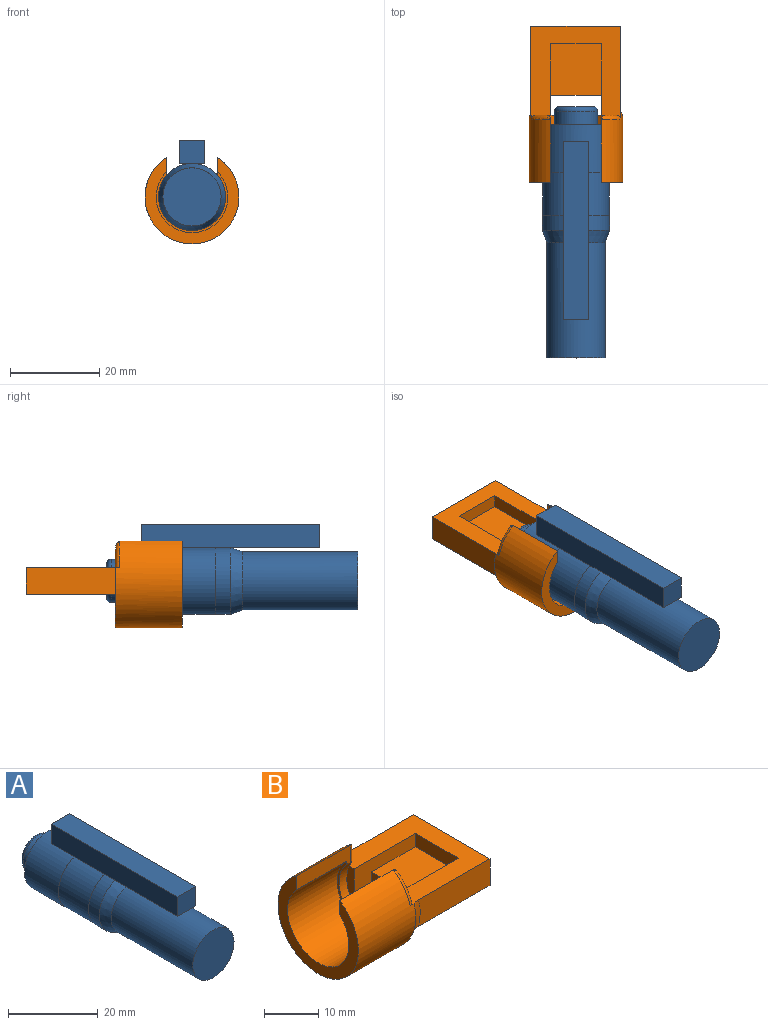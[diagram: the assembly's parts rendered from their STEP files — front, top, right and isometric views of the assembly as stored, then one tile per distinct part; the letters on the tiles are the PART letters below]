
ASSEMBLY  parts=2 mates=1
PART A: 18 faces, bbox 15x56.2x20.2 mm
  f0: cylinder r=7.5mm len=15mm, axis (0,1,0), area 487.2mm2, adj f1,f9,f12,f13
  f1: plane 15x14.9mm, normal (0,-1,0), area 3.4mm2, adj f0,f2,f12
  f2: cylinder r=7.42mm len=14.85mm, axis (0,1,0), area 433.9mm2, adj f1,f4,f12
  f3: cylinder r=7.5mm len=15mm, axis (0,1,0), area 149.7mm2, adj f4,f5,f12
  f4: plane 15x14.9mm, normal (0,1,0), area 3.4mm2, adj f2,f3,f12
  f5: cone r=7.5mm half-angle=20deg, axis (0,1,0), area 128.2mm2, adj f3,f10,f12
  f6: cylinder r=4.83mm len=9.65mm, axis (0,1,0), area 92.5mm2, adj f8,f9
  f7: plane 7.65x7.65mm, normal (0,1,0), area 46mm2, adj f8
  f8: torus R=3.82mm, axis (0,-1,0), area 44mm2, adj f6,f7
  f9: plane 15x15mm, normal (0,1,0), area 103.6mm2, adj f0,f6
  f10: cylinder r=6.5mm len=25.8mm, axis (0,1,0), area 1053.7mm2, adj f5,f11
  f11: plane 13x13mm, normal (0,-1,0), area 132.7mm2, adj f10
  f12: plane 39.9x5.75mm, normal (0,0,-1), area 192.2mm2, adj f0,f1,f2,f3,f4,f5,f13,f14
  f13: plane 5.75x5.3mm, normal (0,1,0), area 30.3mm2, adj f0,f12,f14,f16,f17
  f14: plane 39.9x5.3mm, normal (-1,0,0), area 211.5mm2, adj f12,f13,f15,f17
  f15: plane 5.75x5.3mm, normal (0,-1,0), area 30.5mm2, adj f12,f14,f16,f17
  f16: plane 39.9x5.3mm, normal (1,0,0), area 211.5mm2, adj f12,f13,f15,f17
  f17: plane 39.9x5.75mm, normal (0,0,1), area 229.4mm2, adj f13,f14,f15,f16
PART B: 30 faces, bbox 35.8x22.7x21 mm
  f0: plane 6x1.9mm, normal (-1,0,0), area 10.2mm2, adj f2,f10,f15,f22
  f1: plane 11.45x11.2mm, normal (0,0,1), area 128.3mm2, adj f20,f21,f22,f29
  f2: plane 20.61x20.44mm, normal (0,0,-1), area 349.1mm2, adj f0,f5,f12,f13,f16,f17,f18,f19
  f3: plane 3.83x2.41mm, normal (1,0,0), area 5.4mm2, adj f10,f15,f25,f26
  f4: plane 21x19.38mm, normal (-1,0,0), area 115.2mm2, adj f7,f8,f23,f24
  f5: plane 20.12x7.5mm, normal (1,0,0), area 66.5mm2, adj f2,f7,f10
  f6: plane 3.83x2.41mm, normal (1,0,0), area 5.4mm2, adj f10,f15,f27,f28
  f7: cylinder r=10.5mm len=21mm, axis (1,0,0), area 794.6mm2, adj f4,f5,f11,f13,f14,f15,f19,f23
  f8: cylinder r=8mm len=16mm, axis (1,0,0), area 490.3mm2, adj f4,f9,f23,f24
  f9: plane 16x13.71mm, normal (-1,0,0), area 18.1mm2, adj f8,f10,f23,f24
  f10: cylinder r=7.5mm len=15mm, axis (1,0,0), area 68.3mm2, adj f0,f3,f5,f6,f9,f12,f23,f24
  f11: plane 5.72x0.4mm, normal (1,0,0), area 1.5mm2, adj f7,f17
  f12: plane 6x1.9mm, normal (-1,0,0), area 10.2mm2, adj f2,f10,f15,f21
  f13: plane 0.14x0.04mm, normal (-1,0,0), area 0mm2, adj f2,f7,f17
  f14: plane 0.14x0.04mm, normal (-1,0,0), area 0mm2, adj f7,f15,f17
  f15: plane 21.89x21.05mm, normal (0,0,1), area 221.3mm2, adj f0,f3,f6,f7,f12,f14,f16,f17
  f16: plane 18.82x6mm, normal (0,-1,0), area 110.5mm2, adj f2,f15,f18,f19
  f17: plane 20x6mm, normal (0,1,0), area 120mm2, adj f2,f11,f13,f14,f15,f18
  f18: plane 20x6mm, normal (1,0,0), area 120mm2, adj f2,f15,f16,f17
  f19: bspline ~7.84x1.83mm, area 10.9mm2, adj f2,f7,f15,f16
  f20: plane 11.2x3mm, normal (-1,0,0), area 33.6mm2, adj f1,f15,f21,f22
  f21: plane 16x6mm, normal (0,1,0), area 61.7mm2, adj f1,f2,f12,f15,f20,f29
  f22: plane 16x6mm, normal (0,-1,0), area 61.7mm2, adj f0,f1,f2,f15,f20,f29
  f23: plane 13.95x3.89mm, normal (0,1,0), area 44.9mm2, adj f4,f7,f8,f9,f10,f25
  f24: plane 13.95x3.89mm, normal (0,-1,0), area 44.9mm2, adj f4,f7,f8,f9,f10,f28
  f25: cylinder r=1mm len=5.32mm, axis (0,0,1), area 5.6mm2, adj f3,f10,f23,f26
  f26: torus R=9.5mm, axis (-1,0,0), area 9.6mm2, adj f3,f7,f15,f25
  f27: torus R=9.5mm, axis (-1,0,0), area 9.6mm2, adj f6,f7,f15,f28
  f28: cylinder r=1mm len=5.32mm, axis (0,0,-1), area 5.6mm2, adj f6,f10,f24,f27
  f29: plane 11.2x3mm, normal (-1,0,0), area 33.6mm2, adj f1,f2,f21,f22
PLACE A t=(7.5,-10.08,4.02)mm
PLACE B rot(axis=(0,0,1),90deg) t=(7.5,18.72,4.02)mm
MATE slider B.f7 <-> A.f0  axis (0,1,0) through (7.5,-14.05,4.02)mm
